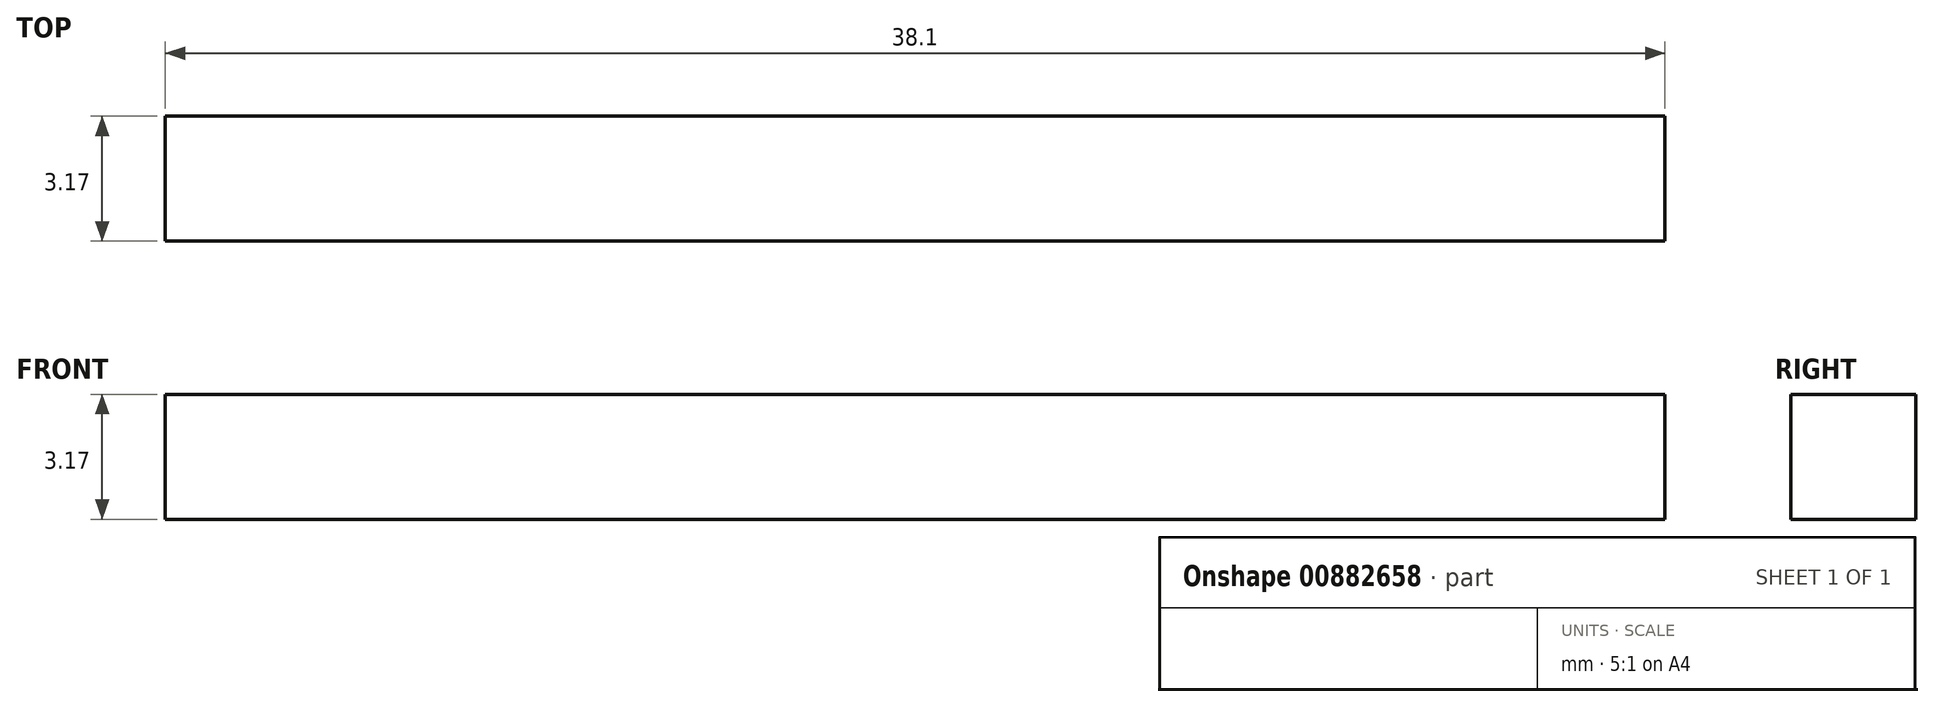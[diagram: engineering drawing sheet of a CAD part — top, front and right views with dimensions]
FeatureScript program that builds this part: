
annotation { "Feature Type Name" : "Feature", "Feature Type Description" : "" }
export const myFeature = defineFeature(function(context is Context, id is Id, definition is map)
    precondition{}
    {
        {
            var Q0;
            Q0=qCreatedBy(makeId("Front.planeOp"),FACE);
            var sketch = newSketch(context, id + "F0", { "sketchPlane" : qUnion([Q0])});
            skLineSegment(sketch, "E0.bottom", {"start": v(60.33, -60.32) * mm, "end": v(-60.33, -60.32) * mm});
            skLineSegment(sketch, "E0.top", {"start": v(60.33, 60.33) * mm, "end": v(-60.33, 60.32) * mm});
            skLineSegment(sketch, "E0.left", {"start": v(60.32, -60.32) * mm, "end": v(60.33, 60.32) * mm});
            skLineSegment(sketch, "E0.right", {"start": v(-60.33, -60.32) * mm, "end": v(-60.32, 60.32) * mm});
            skPoint(sketch, "E0.middle", {"position": v(0, 0) * mm});
            skLineSegment(sketch, "E1", {"start": v(-60.33, 0) * mm, "end": v(-60.33, -19.05) * mm});
            skLineSegment(sketch, "E2", {"start": v(-60.33, -19.05) * mm, "end": v(-57.15, -19.05) * mm});
            skLineSegment(sketch, "E3", {"start": v(-57.15, -19.05) * mm, "end": v(-57.15, -60.32) * mm});
            skLineSegment(sketch, "E4", {"start": v(0, -60.32) * mm, "end": v(-19.05, -60.32) * mm});
            skLineSegment(sketch, "E5.MirrorCS", {"start": v(60.33, -19.05) * mm, "end": v(57.15, -19.05) * mm});
            skLineSegment(sketch, "E6.MirrorCS", {"start": v(57.15, -19.05) * mm, "end": v(57.15, -60.33) * mm});
            skLineSegment(sketch, "E7", {"start": v(-16.51, -57.15) * mm, "end": v(-57.15, -57.15) * mm});
            skLineSegment(sketch, "E8.MirrorCS", {"start": v(19.05, -57.15) * mm, "end": v(57.15, -57.15) * mm});
            skLineSegment(sketch, "E9.MirrorCS", {"start": v(19.05, 57.15) * mm, "end": v(57.15, 57.15) * mm});
            skLineSegment(sketch, "E10.MirrorCS", {"start": v(-19.05, 57.15) * mm, "end": v(-57.15, 57.15) * mm});
            skLineSegment(sketch, "E11.MirrorCS", {"start": v(-19.05, 60.33) * mm, "end": v(-19.05, 57.15) * mm});
            skLineSegment(sketch, "E12.MirrorCS", {"start": v(19.05, 60.33) * mm, "end": v(19.05, 57.15) * mm});
            skLineSegment(sketch, "E13.MirrorCS", {"start": v(-57.15, 19.05) * mm, "end": v(-57.15, 60.33) * mm});
            skLineSegment(sketch, "E14.MirrorCS", {"start": v(57.15, 19.05) * mm, "end": v(57.15, 60.33) * mm});
            skLineSegment(sketch, "E15.MirrorCS", {"start": v(-60.33, 19.05) * mm, "end": v(-57.15, 19.05) * mm});
            skLineSegment(sketch, "E16.MirrorCS", {"start": v(60.32, 19.05) * mm, "end": v(57.15, 19.05) * mm});
            skLineSegment(sketch, "E17", {"start": v(19.05, -57.15) * mm, "end": v(-16.51, -57.15) * mm});
            skLineSegment(sketch, "E18", {"start": v(-19.05, -60.32) * mm, "end": v(-19.05, -57.15) * mm});
            skLineSegment(sketch, "E19", {"start": v(0, -60.32) * mm, "end": v(19.05, -60.32) * mm});
            skLineSegment(sketch, "E20", {"start": v(19.05, -60.32) * mm, "end": v(19.05, -57.15) * mm});
            skLineSegment(sketch, "E21", {"start": v(-19.05, -60.32) * mm, "end": v(19.05, -60.32) * mm});
            skSolve(sketch);
        }
        {
            var Q0;
            {var subQ2=sQuery(id+"F0.wireOp",EDGE,"E1");Q0=makeQuery(id+"F0.imprint","IMPRINT",FACE,{"disambiguationData":[TD([[makeQuery(id+"F0.imprint","IMPRINT",EDGE,{"derivedFrom":subQ2}),1.0]])]});}
            var Q1;
            {var subQ1=sQuery(id+"F0.wireOp",EDGE,"E17");Q1=makeQuery(id+"F0.imprint","IMPRINT",FACE,{"disambiguationData":[TD([[makeQuery(id+"F0.imprint","IMPRINT",EDGE,{"derivedFrom":subQ1}),1.0]])]});}
            extrude(context, id + "F1", {"entities" : qUnion([Q0, Q1]), "depth" : 3.17 * mm, "offsetDistance" : 25.4 * mm});
        }
        {
            var Q0;
            Q0=makeQuery(id+"F1.opExtrude","CAP_FACE",FACE,{"disambiguationData":[OSD([sQuery(id+"F0.wireOp",EDGE,"E0.top"),sQuery(id+"F0.wireOp",EDGE,"E0.left"),sQuery(id+"F0.wireOp",EDGE,"E0.right"),sQuery(id+"F0.wireOp",EDGE,"E1"),sQuery(id+"F0.wireOp",EDGE,"E2"),sQuery(id+"F0.wireOp",EDGE,"E3"),sQuery(id+"F0.wireOp",EDGE,"E5.MirrorCS"),sQuery(id+"F0.wireOp",EDGE,"E6.MirrorCS"),sQuery(id+"F0.wireOp",EDGE,"E7"),sQuery(id+"F0.wireOp",EDGE,"E8.MirrorCS"),sQuery(id+"F0.wireOp",EDGE,"E9.MirrorCS"),sQuery(id+"F0.wireOp",EDGE,"E10.MirrorCS"),sQuery(id+"F0.wireOp",EDGE,"E11.MirrorCS"),sQuery(id+"F0.wireOp",EDGE,"E12.MirrorCS"),sQuery(id+"F0.wireOp",EDGE,"E13.MirrorCS"),sQuery(id+"F0.wireOp",EDGE,"E14.MirrorCS"),sQuery(id+"F0.wireOp",EDGE,"E15.MirrorCS"),sQuery(id+"F0.wireOp",EDGE,"E16.MirrorCS"),sQuery(id+"F0.wireOp",EDGE,"E18"),sQuery(id+"F0.wireOp",EDGE,"E20"),sQuery(id+"F0.wireOp",EDGE,"E21")])],"isStart":false});
            var sketch = newSketch(context, id + "F2", { "sketchPlane" : qUnion([Q0])});
            skLineSegment(sketch, "E22", {"start": v(11.81, -17.53) * mm, "end": v(43.56, -17.53) * mm});
            skLineSegment(sketch, "E23", {"start": v(43.56, -17.53) * mm, "end": v(43.56, 14.22) * mm});
            skLineSegment(sketch, "E24", {"start": v(43.56, 14.22) * mm, "end": v(11.81, 14.22) * mm});
            skLineSegment(sketch, "E25", {"start": v(11.81, 14.22) * mm, "end": v(11.81, -17.53) * mm});
            skSolve(sketch);
        }
        {
            var Q0;
            Q0=makeQuery(id+"F2.imprint","IMPRINT",FACE,{"disambiguationData":[TD([[makeQuery(id+"F2.imprint","IMPRINT",EDGE,{"derivedFrom":sQuery(id+"F2.wireOp",EDGE,"E22")}),1.0]])]});
            extrude(context, id + "F3", {"entities" : qUnion([Q0]), "operationType" : NewBodyOperationType.REMOVE, "endBound" : BoundingType.THROUGH_ALL, "oppositeDirection" : true, "depth" : 25.4 * mm, "offsetDistance" : 25.4 * mm});
        }
    });
